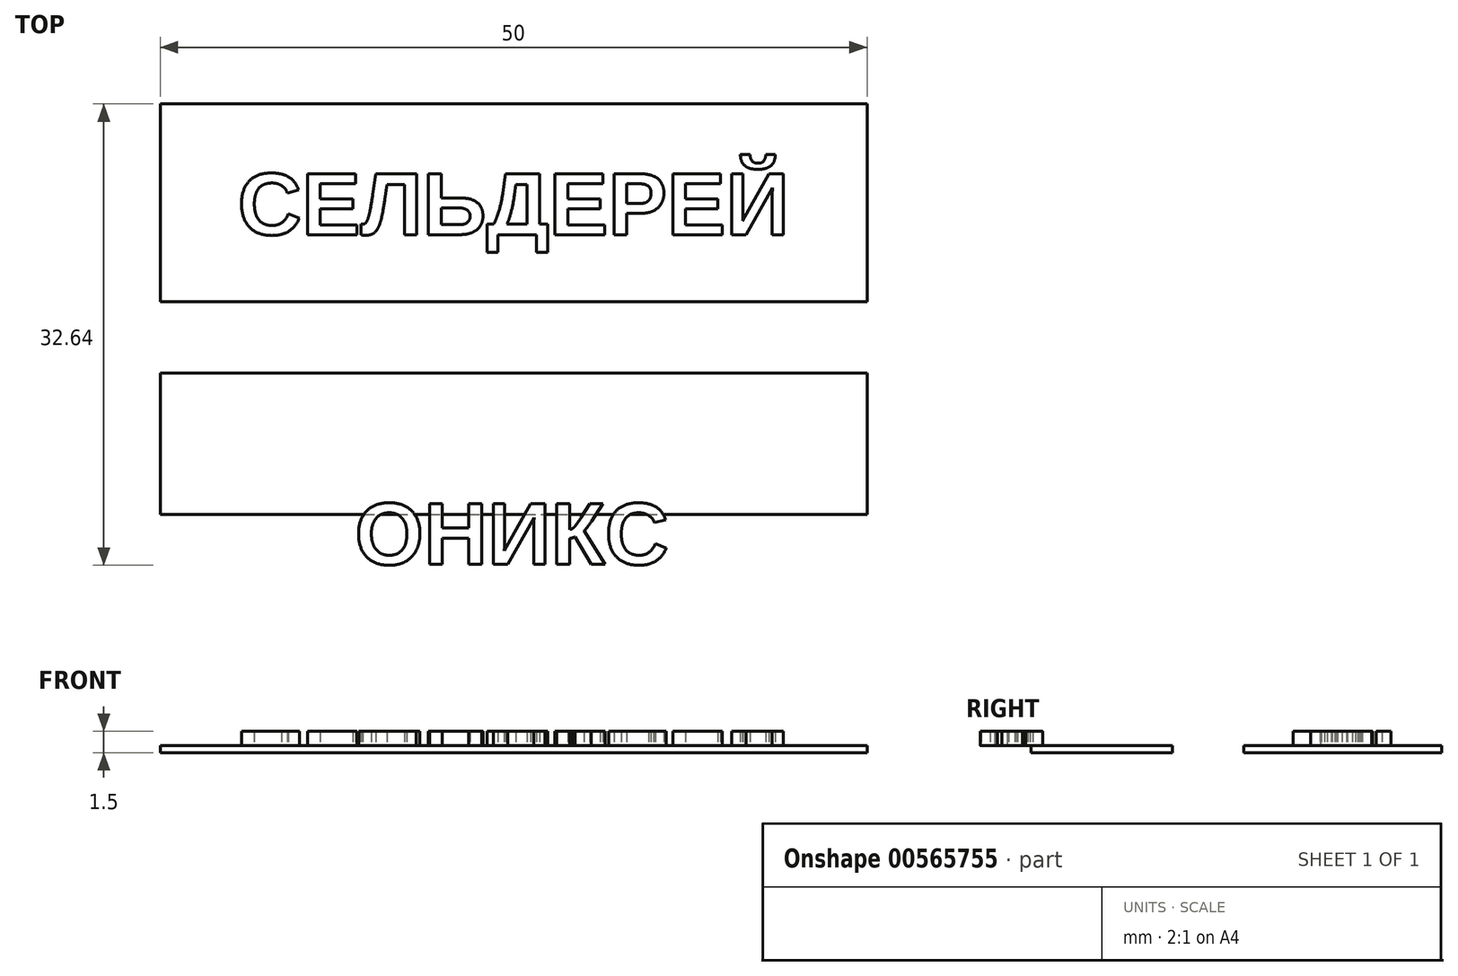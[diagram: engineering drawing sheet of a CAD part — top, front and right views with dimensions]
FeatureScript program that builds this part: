
annotation { "Feature Type Name" : "Feature", "Feature Type Description" : "" }
export const myFeature = defineFeature(function(context is Context, id is Id, definition is map)
    precondition{}
    {
        {
            var Q0;
            Q0=qCreatedBy(makeId("Top.planeOp"),FACE);
            var sketch = newSketch(context, id + "F0", { "sketchPlane" : qUnion([Q0])});
            skLineSegment(sketch, "E0.bottom", {"start": v(-26.49, 21.89) * mm, "end": v(23.51, 21.89) * mm});
            skLineSegment(sketch, "E0.top", {"start": v(-26.49, 7.89) * mm, "end": v(23.51, 7.89) * mm});
            skLineSegment(sketch, "E0.left", {"start": v(-26.49, 21.89) * mm, "end": v(-26.49, 7.89) * mm});
            skLineSegment(sketch, "E0.right", {"start": v(23.51, 21.89) * mm, "end": v(23.51, 7.89) * mm});
            skLineSegment(sketch, "E1.bottom", {"start": v(-26.49, 2.86) * mm, "end": v(23.51, 2.86) * mm});
            skLineSegment(sketch, "E1.top", {"start": v(-26.49, -7.14) * mm, "end": v(23.51, -7.14) * mm});
            skLineSegment(sketch, "E1.left", {"start": v(-26.49, 2.86) * mm, "end": v(-26.49, -7.14) * mm});
            skLineSegment(sketch, "E1.right", {"start": v(23.51, 2.86) * mm, "end": v(23.51, -7.14) * mm});
            skSolve(sketch);
        }
        {
            var Q0;
            Q0 = qSketchRegion(id + "F0", true);
            extrude(context, id + "F1", {"entities" : qUnion([Q0]), "depth" : .5 * mm, "offsetDistance" : 25 * mm});
        }
        {
            var Q0;
            Q0=makeQuery(id+"F1.opExtrude","CAP_FACE",FACE,{"disambiguationData":[OSD([sQuery(id+"F0.wireOp",EDGE,"E0.bottom"),sQuery(id+"F0.wireOp",EDGE,"E0.top"),sQuery(id+"F0.wireOp",EDGE,"E0.left"),sQuery(id+"F0.wireOp",EDGE,"E0.right")])],"isStart":false});
            var sketch = newSketch(context, id + "F2", { "sketchPlane" : qUnion([Q0])});
            skText(sketch, "E2", { "text": "СЕЛЬДЕРЕЙ", "fontName": "Arimo-Bold.ttf"});
            skLineSegment(sketch, "E3", {"start": v(-1.49, 21.89) * mm, "end": v(-1.49, 7.89) * mm, "construction": true});
            skPoint(sketch, "E4", {"position": v(-1.49, 14.89) * mm});
            const initialGuessF2  = {"E2": [-0.021, 0.01264, 1, 0, 0.0045]};
            skSetInitialGuess(sketch, initialGuessF2);
            skSolve(sketch);
        }
        {
            var Q0;
            Q0=makeQuery(id+"F1.opExtrude","CAP_FACE",FACE,{"disambiguationData":[OSD([sQuery(id+"F0.wireOp",EDGE,"E1.bottom"),sQuery(id+"F0.wireOp",EDGE,"E1.top"),sQuery(id+"F0.wireOp",EDGE,"E1.left"),sQuery(id+"F0.wireOp",EDGE,"E1.right")])],"isStart":false});
            var sketch = newSketch(context, id + "F3", { "sketchPlane" : qUnion([Q0])});
            skLineSegment(sketch, "E5", {"start": v(-1.49, 2.86) * mm, "end": v(-1.49, -7.14) * mm, "construction": true});
            skText(sketch, "E6", { "text": "ОНИКС", "fontName": "Arimo-Bold.ttf"});
            skPoint(sketch, "E7", {"position": v(-1.49, -2.14) * mm});
            const initialGuessF3  = {"E6": [-0.01272, -0.01069, 1, 0, 0.0045]};
            skSetInitialGuess(sketch, initialGuessF3);
            skSolve(sketch);
        }
        {
            var Q0;
            Q0 = qSketchRegion(id + "F2", true);
            extrude(context, id + "F4", {"entities" : qUnion([Q0]), "operationType" : NewBodyOperationType.ADD, "depth" : 1 * mm, "offsetDistance" : 25 * mm});
        }
        {
            var Q0;
            Q0 = qSketchRegion(id + "F3", true);
            extrude(context, id + "F5", {"entities" : qUnion([Q0]), "operationType" : NewBodyOperationType.ADD, "depth" : 1 * mm, "offsetDistance" : 25 * mm});
        }
    });
